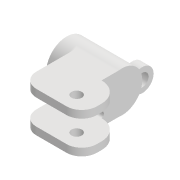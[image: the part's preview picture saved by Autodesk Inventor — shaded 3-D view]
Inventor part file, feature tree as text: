
AUTODESK INVENTOR PART (.ipt)
format: ipt  version: 2022 (Build 260153000, 153)  size: 209,920 bytes
history: native  units: mm
features: extrude x7, sketch x7, fillet x3, projected_geometry x2, mirror x1
ambient origin geometry x8: Origin, YZ Plane, XZ Plane, XY Plane, X Axis, Y Axis, Z Axis, Center Point
bodies: Solid1 (feature_tree)
feature tree (20):
  extrude  "Extrusion1"  Depth=12.2mm
  extrude  "Extrusion2"  Depth=20.0mm TaperAngle=0.0deg
  sketch  "Sketch6"  dims[d5=2.0mm d6=0.0mm d57=5.0mm]
  extrude  "Extrusion9"  Depth=5.0mm
  extrude  "Extrusion10"  Depth=24.0mm
  fillet  "Fillet5"  Radius=8.0mm
  fillet  "Fillet6"  Radius=4.1mm
  mirror  "Mirror1"
  extrude  "Extrusion11"  Depth=6.0mm
  extrude  "Extrusion12"  Depth=6.0mm
  fillet  "Fillet7"  Radius=1.0mm
  extrude  "Extrusion13"  Depth=4.0mm
  sketch  "Sketch1"  dims[d0=9.8mm d1=12.2mm]
  sketch  "Sketch2"  dims[d2=2.0mm d3=20.0mm d4=0.0mm]
  projected_geometry  "Projected Loop1"
  projected_geometry  "Projected Loop2"
  sketch  "Sketch11"  dims[d58=3.0mm d60=24.0mm d61=8.0mm d62=0.0mm d63=4.1mm]
  sketch  "Sketch12"  dims[d64=8.0mm d65=6.0mm]
  sketch  "Sketch14"  dims[d66=32.0mm d67=0.0mm d68=6.0mm d69=1.0mm]
  sketch  "Sketch15"  dims[d70=16.2mm d71=16.2mm d72=100.0mm d73=0.0mm d74=100.0mm d75=0.0mm d76=8.0mm d77=16.0mm d78=0.0mm d79=5.0mm d80=2.0mm d81=4.0mm d82=0.0mm]
